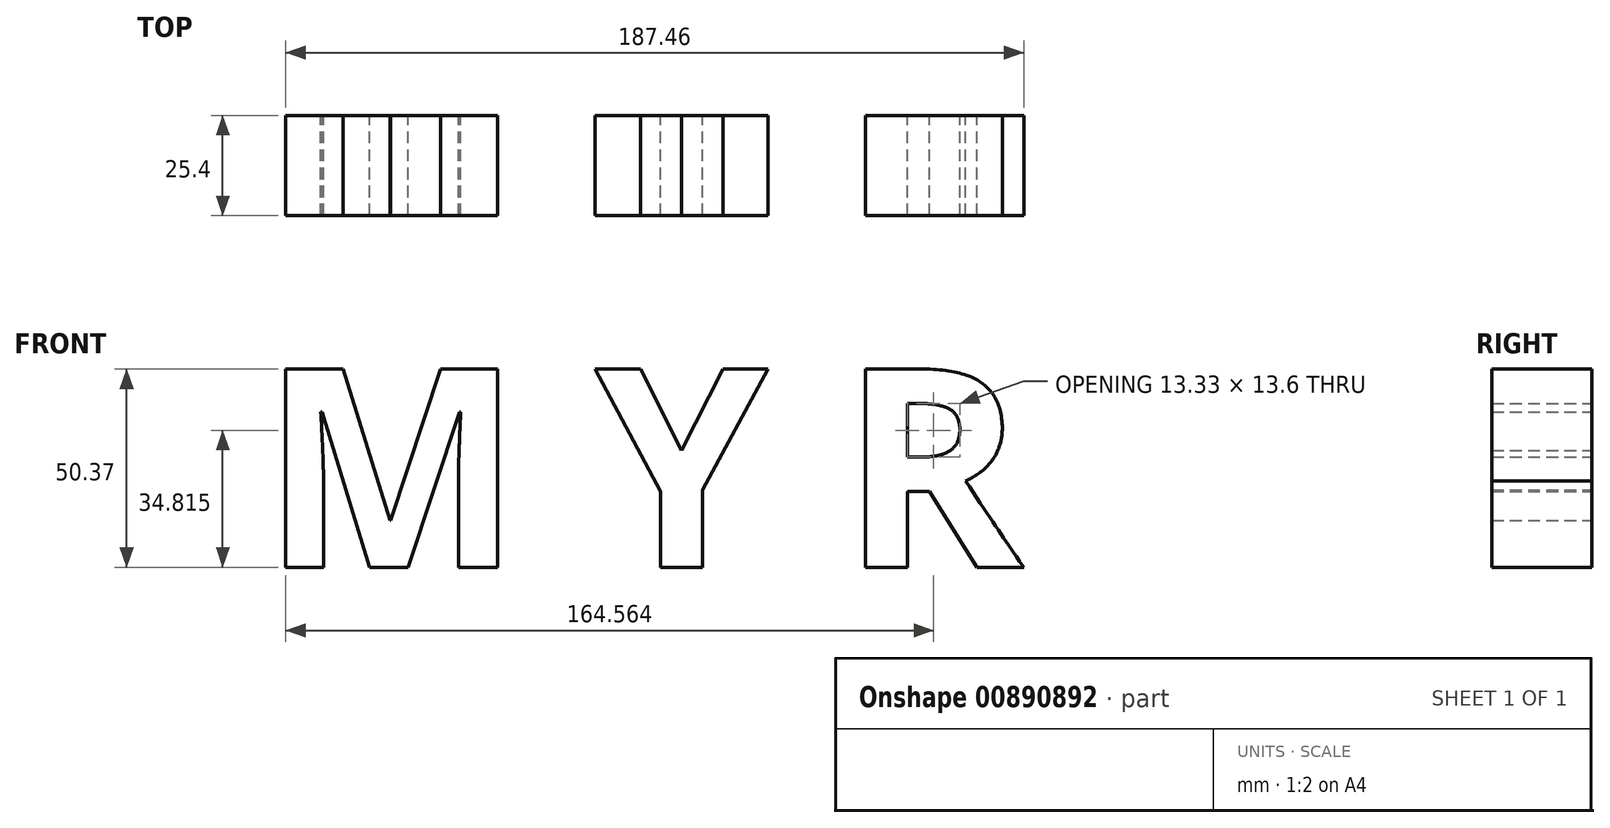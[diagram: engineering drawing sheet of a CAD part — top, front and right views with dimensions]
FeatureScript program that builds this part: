
annotation { "Feature Type Name" : "Feature", "Feature Type Description" : "" }
export const myFeature = defineFeature(function(context is Context, id is Id, definition is map)
    precondition{}
    {
        {
            var Q0;
            Q0=qCreatedBy(makeId("Front.planeOp"),FACE);
            var sketch = newSketch(context, id + "F0", { "sketchPlane" : qUnion([Q0])});
            skText(sketch, "E0", { "text": "M Y R", "fontName": "OpenSans-Bold.ttf"});
            const initialGuessF0  = {"E0": [-0.07756, -0.02583, 1, 0, 0.0508]};
            skSetInitialGuess(sketch, initialGuessF0);
            skSolve(sketch);
        }
        {
            var Q0;
            Q0 = qSketchRegion(id + "F0", true);
            extrude(context, id + "F1", {"entities" : qUnion([Q0]), "depth" : 25.4 * mm, "offsetDistance" : 25.4 * mm});
        }
    });
